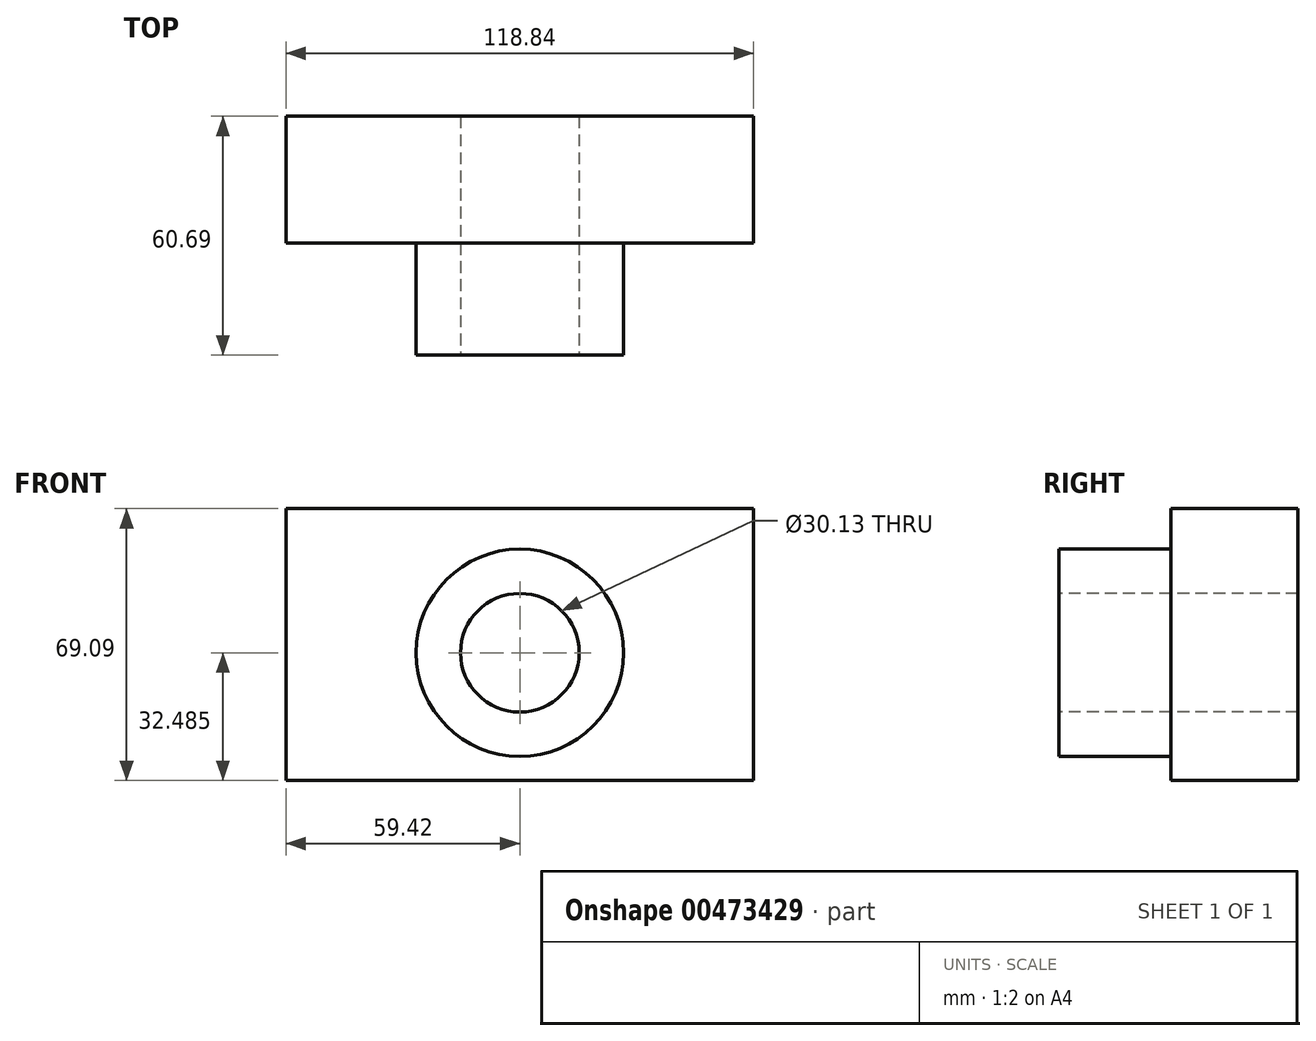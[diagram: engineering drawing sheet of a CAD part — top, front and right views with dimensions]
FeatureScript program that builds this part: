
annotation { "Feature Type Name" : "Feature", "Feature Type Description" : "" }
export const myFeature = defineFeature(function(context is Context, id is Id, definition is map)
    precondition{}
    {
        {
            var Q0;
            Q0=qCreatedBy(makeId("Top.planeOp"),FACE);
            var sketch = newSketch(context, id + "F0", { "sketchPlane" : qUnion([Q0])});
            skLineSegment(sketch, "E0.bottom", {"start": v(59.42, -16.12) * mm, "end": v(-59.42, -16.12) * mm});
            skLineSegment(sketch, "E0.top", {"start": v(59.42, 16.12) * mm, "end": v(-59.42, 16.12) * mm});
            skLineSegment(sketch, "E0.left", {"start": v(59.42, -16.12) * mm, "end": v(59.42, 16.12) * mm});
            skLineSegment(sketch, "E0.right", {"start": v(-59.42, -16.12) * mm, "end": v(-59.42, 16.12) * mm});
            skPoint(sketch, "E0.middle", {"position": v(0, 0) * mm});
            skSolve(sketch);
        }
        {
            var Q0;
            Q0 = qSketchRegion(id + "F0", true);
            extrude(context, id + "F1", {"entities" : qUnion([Q0]), "depth" : 69.1 * mm});
        }
        {
            var Q0;
            Q0=makeQuery(id+"F1.opExtrude","SWEPT_FACE",FACE,{"disambiguationData":[OSD([sQuery(id+"F0.wireOp",EDGE,"E0.bottom")])]});
            var sketch = newSketch(context, id + "F2", { "sketchPlane" : qUnion([Q0])});
            skCircle(sketch, "E1", {"center": v(0, 32.48) * mm, "radius": 15.06 * mm});
            skCircle(sketch, "E2", {"center": v(0, 32.48) * mm, "radius": 26.34 * mm});
            skSolve(sketch);
        }
        {
            var Q0;
            Q0=makeQuery(id+"F2.imprint","IMPRINT",FACE,{"disambiguationData":[TD([[makeQuery(id+"F2.imprint","IMPRINT",EDGE,{"derivedFrom":sQuery(id+"F2.wireOp",EDGE,"E1")}),1.0]])]});
            extrude(context, id + "F3", {"entities" : qUnion([Q0]), "operationType" : NewBodyOperationType.REMOVE, "oppositeDirection" : true, "depth" : 104.65 * mm});
        }
        {
            var Q0;
            Q0 = qSketchRegion(id + "F2", true);
            extrude(context, id + "F4", {"entities" : qUnion([Q0]), "operationType" : NewBodyOperationType.ADD, "depth" : 28.45 * mm});
        }
    });
